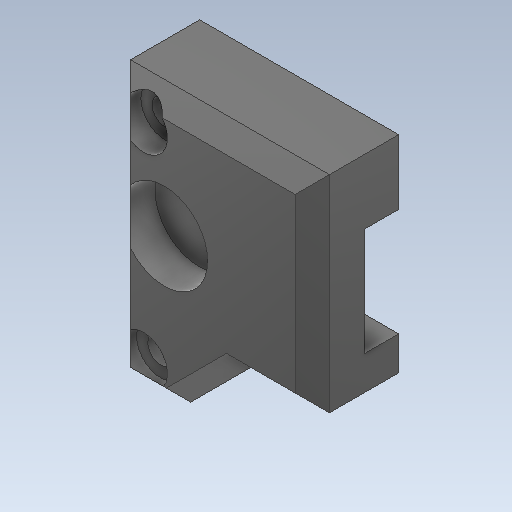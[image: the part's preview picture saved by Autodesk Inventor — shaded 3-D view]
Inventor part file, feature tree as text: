
AUTODESK INVENTOR PART (.ipt)
format: ipt  version: 2020 (Build 240168000, 168)  size: 248,832 bytes
history: native  units: in
note: dims shown in document units (in); Inventor stores cm internally (conversion verified against a paired STEP export)
features: sketch x30, other x3, plane x1
ambient origin geometry x8: Origin, YZ Plane, XZ Plane, XY Plane, X Axis, Y Axis, Z Axis, Center Point
bodies: Solid1 (feature_tree)
feature tree (34):
  other  "FermurSupportSup.ipt"
  other  "Solid1::FermurSupportSup.ipt"
  other  "TaggingFeature1"
  sketch  "Sketch1"  dims[d0=0.3937in]
  sketch  "Sketch2"
  sketch  "Sketch3"
  sketch  "Sketch4"
  sketch  "Sketch5"
  sketch  "Sketch6"
  sketch  "Sketch8"
  sketch  "Sketch10"
  sketch  "Sketch11"
  sketch  "Sketch12"
  sketch  "Sketch13"
  sketch  "Sketch14"
  sketch  "Sketch15"
  sketch  "Sketch17"
  sketch  "Sketch19"
  sketch  "Sketch21"
  sketch  "Sketch22"
  sketch  "Sketch23"
  sketch  "Sketch24"
  sketch  "Sketch25"
  sketch  "Sketch26"
  sketch  "Sketch27"
  sketch  "Sketch29"
  sketch  "Sketch32"
  sketch  "Sketch33"
  sketch  "Sketch36"
  sketch  "Sketch37"
  sketch  "Sketch38"
  sketch  "Sketch39"
  sketch  "Sketch40"
  plane  "Work Plane1"
